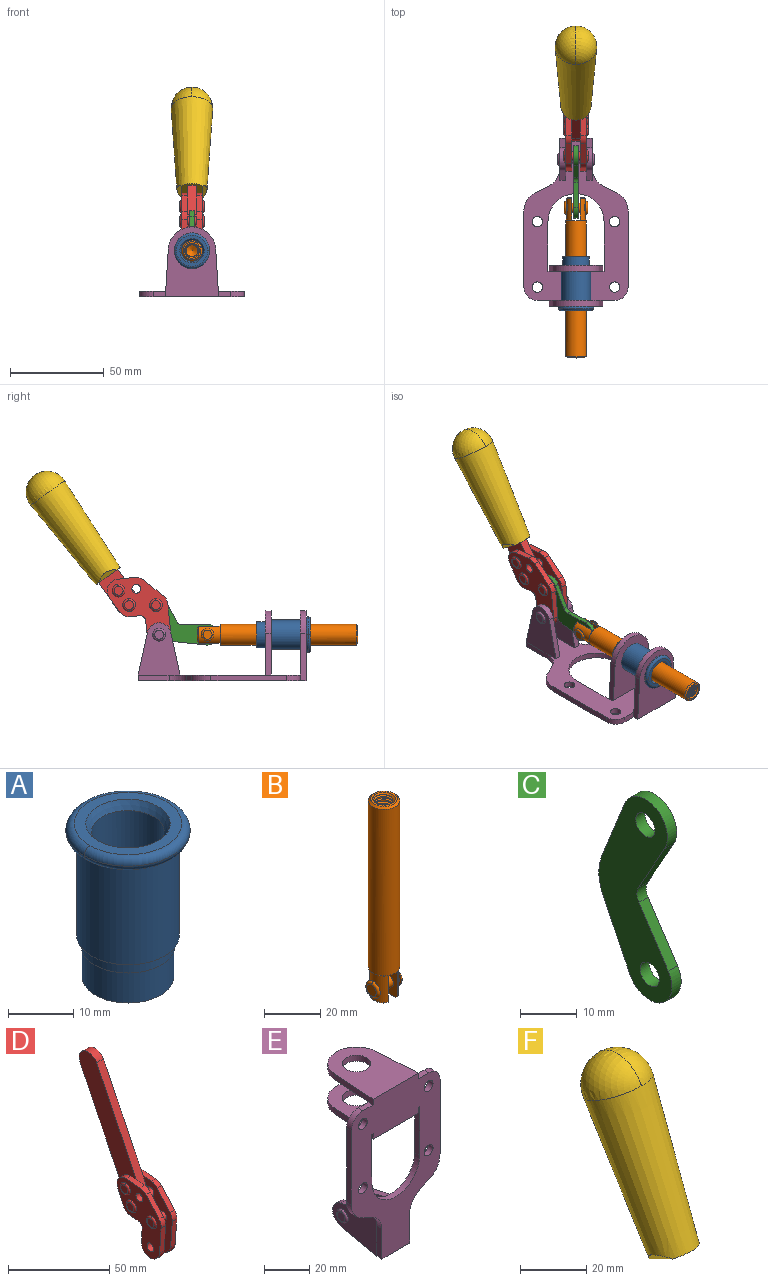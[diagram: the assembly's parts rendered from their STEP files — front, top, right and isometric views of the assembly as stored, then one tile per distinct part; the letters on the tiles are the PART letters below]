
ASSEMBLY  parts=6 mates=6
PART A: 15 faces, bbox 20.6x20.6x28.7 mm
  f0: torus R=8.26mm, axis (0,0,1), area 56.8mm2, adj f1,f10,f12
  f1: torus R=8.26mm, axis (0,0,1), area 56.8mm2, adj f0,f6,f13
  f2: cylinder r=5.59mm len=25.91mm, axis (0,0,1), area 909.6mm2, adj f3,f4
  f3: cone r=6.86mm half-angle=45deg, axis (0,0,-1), area 70.2mm2, adj f2,f14
  f4: cone r=6.47mm half-angle=30deg, axis (0,0,1), area 66.7mm2, adj f2,f13
  f5: cylinder r=7.04mm len=14.07mm, axis (0,0,1), area 252.6mm2, adj f11,f14
  f6: torus R=8.26mm, axis (0,0,1), area 56.8mm2, adj f1,f12,f13
  f7: cylinder r=7.16mm len=14.33mm, axis (0,0,1), area 91.5mm2, adj f9,f11
  f8: cylinder r=7.86mm len=18.42mm, axis (0,0,1), area 909.6mm2, adj f9,f10
  f9: plane 15.72x15.72mm, normal (0,0,-1), area 33mm2, adj f7,f8
  f10: plane 16.51x16.51mm, normal (0,0,-1), area 19.9mm2, adj f0,f8,f12
  f11: plane 14.33x14.33mm, normal (0,0,-1), area 5.7mm2, adj f5,f7
  f12: torus R=8.26mm, axis (0,0,1), area 56.8mm2, adj f0,f6,f10
  f13: plane 16.51x16.51mm, normal (0,0,1), area 82.7mm2, adj f1,f4,f6
  f14: plane 14.07x14.07mm, normal (0,0,-1), area 7.8mm2, adj f3,f5
PART B: 48 faces, bbox 12.6x11.1x86.1 mm
  f0: torus R=2.41mm, axis (-1,0,0), area 15mm2, adj f30,f32,f34
  f1: torus R=2.41mm, axis (-1,0,0), area 15mm2, adj f29,f31,f33
  f2: cylinder r=5.54mm len=72.39mm, axis (0,0,1), area 2518.5mm2, adj f3,f4,f42,f43
  f3: cone r=5.54mm half-angle=45deg, axis (0,0,1), area 7.6mm2, adj f2,f5,f41
  f4: cone r=5.54mm half-angle=45deg, axis (0,0,-1), area 34.9mm2, adj f2,f39
  f5: cylinder r=5.08mm len=11.48mm, axis (0,0,1), area 108.3mm2, adj f3,f7,f8,f41
  f6: cylinder r=2.41mm len=4.83mm, axis (-1,0,0), area 71.2mm2, adj f40,f41
  f7: cylinder r=2.41mm len=4.83mm, axis (-1,0,0), area 7.6mm2, adj f5,f34
  f8: cone r=5.08mm half-angle=45deg, axis (0,0,1), area 10.6mm2, adj f5,f37,f41
  f9: cone r=3.98mm half-angle=45deg, axis (0,0,1), area 17.6mm2, adj f27,f39,f45,f46,f47
  f10: cylinder r=2.41mm len=4.83mm, axis (-1,0,0), area 7.6mm2, adj f33,f38
  f11: cylinder r=3.2mm len=6.4mm, axis (0,0,1), area 78.4mm2, adj f12,f28,f44,f45,f47
  f12: cylinder r=3.2mm len=6.4mm, axis (0,0,1), area 10.5mm2, adj f11,f13,f45,f47
  f13: cylinder r=3.2mm len=6.4mm, axis (0,0,1), area 10.5mm2, adj f12,f14,f45,f47
  f14: cylinder r=3.2mm len=6.4mm, axis (0,0,1), area 10.5mm2, adj f13,f15,f45,f47
  f15: cylinder r=3.2mm len=6.4mm, axis (0,0,1), area 10.5mm2, adj f14,f16,f45,f47
  f16: cylinder r=3.2mm len=6.4mm, axis (0,0,1), area 10.5mm2, adj f15,f17,f45,f47
  f17: cylinder r=3.2mm len=6.4mm, axis (0,0,1), area 10.5mm2, adj f16,f18,f45,f47
  f18: cylinder r=3.2mm len=6.4mm, axis (0,0,1), area 10.5mm2, adj f17,f19,f45,f47
  f19: cylinder r=3.2mm len=6.4mm, axis (0,0,1), area 10.5mm2, adj f18,f20,f45,f47
  f20: cylinder r=3.2mm len=6.4mm, axis (0,0,1), area 10.5mm2, adj f19,f21,f45,f47
  f21: cylinder r=3.2mm len=6.4mm, axis (0,0,1), area 10.5mm2, adj f20,f22,f45,f47
  f22: cylinder r=3.2mm len=6.4mm, axis (0,0,1), area 10.5mm2, adj f21,f23,f45,f47
  f23: cylinder r=3.2mm len=6.4mm, axis (0,0,1), area 10.5mm2, adj f22,f24,f45,f47
  f24: cylinder r=3.2mm len=6.4mm, axis (0,0,1), area 10.5mm2, adj f23,f25,f45,f47
  f25: cylinder r=3.2mm len=6.4mm, axis (0,0,1), area 10.5mm2, adj f24,f26,f45,f47
  f26: cylinder r=3.2mm len=6.4mm, axis (0,0,1), area 10.5mm2, adj f25,f27,f45,f47
  f27: cylinder r=3.2mm len=6.4mm, axis (0,0,1), area 7.4mm2, adj f9,f26,f45,f47
  f28: cone r=3.2mm half-angle=60deg, axis (0,0,1), area 37.2mm2, adj f11
  f29: plane 4.83x4.83mm, normal (-1,0,0), area 18.3mm2, adj f1,f31
  f30: plane 4.83x4.83mm, normal (1,0,0), area 18.3mm2, adj f0,f32
  f31: torus R=2.41mm, axis (-1,0,0), area 15mm2, adj f1,f29,f33
  f32: torus R=2.41mm, axis (-1,0,0), area 15mm2, adj f0,f30,f34
  f33: plane 6.83x6.83mm, normal (1,0,0), area 18.3mm2, adj f1,f10,f31
  f34: plane 6.83x6.83mm, normal (-1,0,0), area 18.3mm2, adj f0,f7,f32
  f35: cone r=5.08mm half-angle=45deg, axis (0,0,1), area 10.6mm2, adj f36,f38,f40
  f36: plane 7.25x1.97mm, normal (0,0,-1), area 10mm2, adj f35,f40
  f37: plane 7.25x1.97mm, normal (0,0,-1), area 10mm2, adj f8,f41
  f38: cylinder r=5.08mm len=11.48mm, axis (0,0,1), area 108.3mm2, adj f10,f35,f40,f42
  f39: plane 9.55x9.55mm, normal (0,0,1), area 22mm2, adj f4,f9
  f40: plane 12.76x10.09mm, normal (1,0,0), area 95.7mm2, adj f6,f35,f36,f38,f42,f43
  f41: plane 12.76x10.09mm, normal (-1,0,0), area 95.7mm2, adj f3,f5,f6,f8,f37,f43
  f42: cone r=5.54mm half-angle=45deg, axis (0,0,1), area 7.6mm2, adj f2,f38,f40
  f43: plane 11.07x4.7mm, normal (0,0,-1), area 50.4mm2, adj f2,f40,f41
  f44: plane 0.89x0.62mm, normal (-1,0,0), area 0.3mm2, adj f11,f45,f46,f47
  f45: bspline ~24.8x7.63mm, area 266.6mm2, adj f9,f11,f12,f13,f14,f15,f16,f17
  f46: bspline ~24.87x7.63mm, area 73.6mm2, adj f9,f44,f45,f47
  f47: bspline ~24.98x7.63mm, area 272.5mm2, adj f9,f11,f12,f13,f14,f15,f16,f17
PART C: 12 faces, bbox 2.3x18.2x42.8 mm
  f0: cylinder r=2.4mm len=4.8mm, axis (1,0,0), area 34.9mm2, adj f4,f11
  f1: cylinder r=10.41mm len=8.47mm, axis (1,0,0), area 20.2mm2, adj f4,f9,f10,f11
  f2: cylinder r=3.05mm len=3.16mm, axis (1,0,0), area 7.7mm2, adj f4,f6,f7,f11
  f3: cylinder r=2.4mm len=4.8mm, axis (1,0,0), area 34.9mm2, adj f4,f11
  f4: plane 42.81x18.23mm, normal (-1,0,0), area 414.1mm2, adj f0,f1,f2,f3,f5,f6,f7,f8
  f5: cylinder r=5.54mm len=10.67mm, axis (1,0,0), area 41.8mm2, adj f4,f6,f10,f11
  f6: plane 11.66x6.53mm, normal (0,-0.87,-0.49), area 30.9mm2, adj f2,f4,f5,f11
  f7: plane 11.17x7.33mm, normal (0,-0.84,0.55), area 30.9mm2, adj f2,f4,f8,f11
  f8: cylinder r=5.54mm len=10.51mm, axis (1,0,0), area 41.8mm2, adj f4,f7,f9,f11
  f9: plane 13.67x6.67mm, normal (0,0.9,-0.44), area 35.1mm2, adj f1,f4,f8,f11
  f10: plane 14.1x5.7mm, normal (0,0.93,0.37), area 35.1mm2, adj f1,f4,f5,f11
  f11: plane 42.81x18.23mm, normal (1,0,0), area 414.1mm2, adj f0,f1,f2,f3,f5,f6,f7,f8
PART D: 59 faces, bbox 12.9x60.2x99.6 mm
  f0: torus R=2.39mm, axis (-1,0,0), area 14.9mm2, adj f20,f43,f51
  f1: torus R=2.39mm, axis (-1,0,0), area 14.9mm2, adj f19,f42,f51
  f2: torus R=2.39mm, axis (-1,0,0), area 14.9mm2, adj f18,f35,f51
  f3: torus R=2.39mm, axis (-1,0,0), area 14.9mm2, adj f14,f17,f23
  f4: torus R=2.39mm, axis (-1,0,0), area 14.9mm2, adj f13,f16,f23
  f5: torus R=2.39mm, axis (-1,0,0), area 14.9mm2, adj f12,f15,f23
  f6: cylinder r=2.39mm len=4.78mm, axis (1,0,0), area 46.5mm2, adj f48,f50,f51
  f7: cylinder r=2.39mm len=4.78mm, axis (1,0,0), area 46.5mm2, adj f50,f51
  f8: cylinder r=6.35mm len=12.68mm, axis (1,0,0), area 61.8mm2, adj f38,f39,f50,f51
  f9: cylinder r=2.39mm len=4.78mm, axis (-1,0,0), area 70.5mm2, adj f46,f50
  f10: cylinder r=2.39mm len=4.78mm, axis (-1,0,0), area 46.5mm2, adj f23,f45,f46
  f11: cylinder r=2.39mm len=4.78mm, axis (-1,0,0), area 46.5mm2, adj f23,f46
  f12: plane 4.78x4.78mm, normal (1,0,0), area 17.9mm2, adj f5,f15
  f13: plane 4.78x4.78mm, normal (1,0,0), area 17.9mm2, adj f4,f16
  f14: plane 4.78x4.78mm, normal (1,0,0), area 17.9mm2, adj f3,f17
  f15: torus R=2.39mm, axis (-1,0,0), area 14.9mm2, adj f5,f12,f23
  f16: torus R=2.39mm, axis (-1,0,0), area 14.9mm2, adj f4,f13,f23
  f17: torus R=2.39mm, axis (-1,0,0), area 14.9mm2, adj f3,f14,f23
  f18: plane 4.78x4.78mm, normal (-1,0,0), area 17.9mm2, adj f2,f35
  f19: plane 4.78x4.78mm, normal (-1,0,0), area 17.9mm2, adj f1,f42
  f20: plane 4.78x4.78mm, normal (-1,0,0), area 17.9mm2, adj f0,f43
  f21: plane 2.26x0.2mm, normal (1,0,0), area 0.2mm2, adj f31,f44
  f22: plane 2.26x0.2mm, normal (-1,0,0), area 0.2mm2, adj f41,f44
  f23: plane 39.37x30.77mm, normal (1,0,0), area 565.5mm2, adj f3,f4,f5,f10,f11,f15,f16,f17
  f24: cylinder r=6.1mm len=4.15mm, axis (-1,0,0), area 14.7mm2, adj f23,f25,f32,f46
  f25: plane 10.25x9.01mm, normal (0,-0.75,0.66), area 42.3mm2, adj f23,f24,f26,f46
  f26: cylinder r=6.35mm len=4.64mm, axis (-1,0,0), area 15.6mm2, adj f23,f25,f27,f46
  f27: plane 15.84x3.1mm, normal (0,-1,-0.07), area 49.2mm2, adj f23,f26,f28,f46
  f28: cylinder r=6.35mm len=12.68mm, axis (-1,0,0), area 61.8mm2, adj f23,f27,f29,f46
  f29: plane 8.11x3.1mm, normal (0,1,0.07), area 25.2mm2, adj f23,f28,f30,f46
  f30: cylinder r=3.05mm len=3.25mm, axis (-1,0,0), area 14.8mm2, adj f23,f29,f31,f46
  f31: plane 5.99x3.1mm, normal (0,0.07,-1), area 18.6mm2, adj f21,f23,f30,f44,f46
  f32: plane 9.5x3.1mm, normal (0,-0.07,1), area 29.5mm2, adj f23,f24,f33,f46,f47
  f33: cylinder r=6.1mm len=8.63mm, axis (-1,0,0), area 39.1mm2, adj f23,f32,f34,f47
  f34: plane 8.65x3.96mm, normal (0,0.91,-0.42), area 29.5mm2, adj f23,f33,f44,f47
  f35: torus R=2.39mm, axis (-1,0,0), area 14.9mm2, adj f2,f18,f51
  f36: plane 10.25x9.01mm, normal (0,-0.75,0.66), area 42.3mm2, adj f37,f49,f50,f51
  f37: cylinder r=6.35mm len=4.64mm, axis (1,0,0), area 15.6mm2, adj f36,f38,f50,f51
  f38: plane 15.84x3.1mm, normal (0,-1,-0.07), area 49.2mm2, adj f8,f37,f50,f51
  f39: plane 8.11x3.1mm, normal (0,1,0.07), area 25.2mm2, adj f8,f40,f50,f51
  f40: cylinder r=3.05mm len=3.25mm, axis (1,0,0), area 14.8mm2, adj f39,f41,f50,f51
  f41: plane 5.99x3.1mm, normal (0,0.07,-1), area 18.6mm2, adj f22,f40,f44,f50,f51
  f42: torus R=2.39mm, axis (-1,0,0), area 14.9mm2, adj f1,f19,f51
  f43: torus R=2.39mm, axis (-1,0,0), area 14.9mm2, adj f0,f20,f51
  f44: cylinder r=6.35mm len=12.12mm, axis (-1,0,0), area 128.9mm2, adj f21,f22,f23,f31,f34,f41,f46,f47
  f45: plane 2.65x1.35mm, normal (1,0,0), area 1mm2, adj f10,f55
  f46: plane 39.08x20.42mm, normal (-1,0,0), area 412.5mm2, adj f9,f10,f11,f24,f25,f26,f27,f28
  f47: plane 77.62x39.82mm, normal (1,0,0), area 850mm2, adj f32,f33,f34,f44,f53,f54,f55
  f48: plane 2.65x1.35mm, normal (-1,0,0), area 1mm2, adj f6,f55
  f49: cylinder r=6.1mm len=4.15mm, axis (1,0,0), area 14.7mm2, adj f36,f50,f51,f56
  f50: plane 39.08x20.42mm, normal (1,0,0), area 412.5mm2, adj f6,f7,f8,f9,f36,f37,f38,f39
  f51: plane 39.37x30.77mm, normal (-1,0,0), area 565.5mm2, adj f0,f1,f2,f6,f7,f8,f35,f36
  f52: plane 8.65x3.96mm, normal (0,0.91,-0.42), area 29.5mm2, adj f44,f51,f57,f58
  f53: plane 68.49x33.4mm, normal (0,0.9,-0.44), area 358.1mm2, adj f44,f47,f54,f58
  f54: cylinder r=6.35mm len=12.06mm, axis (1,0,0), area 93.7mm2, adj f47,f53,f55,f58
  f55: plane 68.49x33.4mm, normal (0,-0.9,0.44), area 358.1mm2, adj f44,f45,f46,f47,f48,f50,f54,f58
  f56: plane 9.5x3.1mm, normal (0,-0.07,1), area 29.5mm2, adj f49,f50,f51,f57,f58
  f57: cylinder r=6.1mm len=8.63mm, axis (1,0,0), area 39.1mm2, adj f51,f52,f56,f58
  f58: plane 77.62x39.82mm, normal (-1,0,0), area 850mm2, adj f44,f52,f53,f54,f55,f56,f57
PART E: 55 faces, bbox 55.7x37.4x89.8 mm
  f0: torus R=2.41mm, axis (-1,0,0), area 15mm2, adj f11,f15,f25
  f1: torus R=2.41mm, axis (-1,0,0), area 15mm2, adj f10,f12,f22
  f2: cylinder r=2.78mm len=5.56mm, axis (0,-1,0), area 54.2mm2, adj f30,f54
  f3: cylinder r=14.99mm len=29.97mm, axis (0,-1,0), area 145.9mm2, adj f30,f49,f53,f54
  f4: cylinder r=2.78mm len=5.56mm, axis (0,-1,0), area 54.2mm2, adj f30,f54
  f5: cylinder r=2.78mm len=5.56mm, axis (0,-1,0), area 54.2mm2, adj f30,f54
  f6: cylinder r=2.78mm len=5.56mm, axis (0,-1,0), area 54.2mm2, adj f30,f54
  f7: cylinder r=6.35mm len=12.7mm, axis (0,0,1), area 123.6mm2, adj f27,f51
  f8: cylinder r=6.35mm len=12.7mm, axis (0,0,-1), area 124.7mm2, adj f21,f35
  f9: cylinder r=2.41mm len=11.18mm, axis (-1,0,0), area 169.4mm2, adj f16,f19
  f10: plane 4.83x4.83mm, normal (1,0,0), area 18.3mm2, adj f1,f12
  f11: plane 4.83x4.83mm, normal (-1,0,0), area 18.3mm2, adj f0,f15
  f12: torus R=2.41mm, axis (-1,0,0), area 15mm2, adj f1,f10,f22
  f13: cylinder r=6.35mm len=12.41mm, axis (1,0,0), area 53.4mm2, adj f18,f19,f22,f23
  f14: cylinder r=6.35mm len=12.41mm, axis (-1,0,0), area 53.4mm2, adj f16,f17,f24,f25
  f15: torus R=2.41mm, axis (-1,0,0), area 15mm2, adj f0,f11,f25
  f16: plane 27.86x22.35mm, normal (1,0,0), area 425.4mm2, adj f9,f14,f17,f24,f30
  f17: plane 22.86x4.97mm, normal (0,0.21,0.98), area 72.5mm2, adj f14,f16,f25,f30
  f18: plane 22.86x4.97mm, normal (0,0.21,0.98), area 72.5mm2, adj f13,f19,f22,f30
  f19: plane 27.86x22.35mm, normal (-1,0,0), area 425.4mm2, adj f9,f13,f18,f23,f30
  f20: cylinder r=12.7mm len=25.35mm, axis (0,0,-1), area 119.8mm2, adj f21,f34,f35,f36
  f21: plane 34.21x28.07mm, normal (0,0,-1), area 702.4mm2, adj f8,f20,f30,f34,f36
  f22: plane 27.96x22.45mm, normal (1,0,0), area 407.2mm2, adj f1,f12,f13,f18,f23,f30,f42,f43
  f23: plane 22.86x4.97mm, normal (0,0.21,-0.98), area 72.5mm2, adj f13,f19,f22,f44
  f24: plane 22.86x4.97mm, normal (0,0.21,-0.98), area 72.5mm2, adj f14,f16,f25,f44
  f25: plane 27.86x22.35mm, normal (-1,0,0), area 407.1mm2, adj f0,f14,f15,f17,f24,f30,f45,f46
  f26: plane 3.1x0.95mm, normal (0,0,-1), area 2.7mm2, adj f30,f49,f50,f54
  f27: plane 34.21x28.07mm, normal (0,0,1), area 702.4mm2, adj f7,f28,f30,f50,f52
  f28: cylinder r=12.7mm len=25.35mm, axis (0,0,1), area 118.8mm2, adj f27,f50,f51,f52
  f29: plane 3.1x0.95mm, normal (0,0,-1), area 2.7mm2, adj f30,f52,f53,f54
  f30: plane 86.54x55.63mm, normal (0,1,0), area 2362.9mm2, adj f2,f3,f4,f5,f6,f16,f17,f18
  f31: plane 40.56x3.1mm, normal (-1,0,0), area 125.7mm2, adj f30,f32,f48,f54
  f32: cylinder r=7.11mm len=7.11mm, axis (0,-1,0), area 34.6mm2, adj f30,f31,f33,f54
  f33: plane 6.67x3.1mm, normal (0,0,1), area 20.4mm2, adj f30,f32,f34,f54
  f34: plane 25.39x3.13mm, normal (-1,0.06,0), area 79.5mm2, adj f20,f21,f33,f35,f54
  f35: plane 37.31x28.45mm, normal (0,0,1), area 789.9mm2, adj f8,f20,f34,f36,f54
  f36: plane 25.39x3.13mm, normal (1,0.06,0), area 79.5mm2, adj f20,f21,f35,f37,f54
  f37: plane 6.67x3.1mm, normal (0,0,1), area 20.4mm2, adj f30,f36,f38,f54
  f38: cylinder r=7.11mm len=7.11mm, axis (0,-1,0), area 34.6mm2, adj f30,f37,f39,f54
  f39: plane 40.56x3.1mm, normal (1,0,0), area 125.7mm2, adj f30,f38,f40,f54
  f40: cylinder r=11.18mm len=10.16mm, axis (0,-1,0), area 39.5mm2, adj f30,f39,f41,f54
  f41: plane 6.09x3.1mm, normal (0.42,0,-0.91), area 20.8mm2, adj f30,f40,f42,f54
  f42: cylinder r=11.18mm len=9.41mm, axis (0,-1,0), area 37.2mm2, adj f22,f30,f41,f43,f54
  f43: plane 16.5x3.1mm, normal (1,0,0), area 51.1mm2, adj f22,f42,f44,f54
  f44: plane 17.37x3.1mm, normal (0,0,-1), area 53.8mm2, adj f23,f24,f30,f43,f45,f54
  f45: plane 16.5x3.1mm, normal (-1,0,0), area 51.1mm2, adj f25,f44,f46,f54
  f46: cylinder r=11.18mm len=9.41mm, axis (0,-1,0), area 37.2mm2, adj f25,f30,f45,f47,f54
  f47: plane 6.09x3.1mm, normal (-0.42,0,-0.91), area 20.8mm2, adj f30,f46,f48,f54
  f48: cylinder r=11.18mm len=10.16mm, axis (0,-1,0), area 39.5mm2, adj f30,f31,f47,f54
  f49: plane 26.54x3.1mm, normal (-1,0,0), area 82.3mm2, adj f3,f26,f30,f54
  f50: plane 25.39x3.1mm, normal (1,0.06,0), area 78.8mm2, adj f26,f27,f28,f51,f54
  f51: plane 37.31x28.45mm, normal (0,0,-1), area 789.9mm2, adj f7,f28,f50,f52,f54
  f52: plane 25.39x3.1mm, normal (-1,0.06,0), area 78.8mm2, adj f27,f28,f29,f51,f54
  f53: plane 26.54x3.1mm, normal (1,0,0), area 82.3mm2, adj f3,f29,f30,f54
  f54: plane 89.66x55.63mm, normal (0,-1,0), area 2678.5mm2, adj f2,f3,f4,f5,f6,f26,f29,f31
PART F: 11 faces, bbox 22.3x42.6x64.5 mm
  f0: sphere r=11.13mm, area 411.4mm2, adj f1,f8
  f1: cone r=11.11mm half-angle=3.3deg, axis (0,0.44,0.9), area 3251.8mm2, adj f0,f7,f8,f9,f10
  f2: cylinder r=6.16mm len=11.7mm, axis (1,0,0), area 89.5mm2, adj f3,f4,f5,f6
  f3: plane 60.23x36.75mm, normal (-1,0,0), area 763.6mm2, adj f2,f4,f6,f10
  f4: plane 51.37x25.05mm, normal (0,0.9,-0.44), area 264.2mm2, adj f2,f3,f5,f10
  f5: plane 60.23x36.75mm, normal (1,0,0), area 763.6mm2, adj f2,f4,f6,f10
  f6: plane 51.37x25.05mm, normal (0,-0.9,0.44), area 264.2mm2, adj f2,f3,f5,f10
  f7: plane 9.95x5.95mm, normal (0.71,-0.31,-0.64), area 25.8mm2, adj f1,f10
  f8: sphere r=11.13mm, area 411.4mm2, adj f0,f1
  f9: plane 9.95x5.95mm, normal (-0.71,-0.31,-0.64), area 25.8mm2, adj f1,f10
  f10: plane 14.27x11.38mm, normal (0,-0.44,-0.9), area 106.7mm2, adj f1,f3,f4,f5,f6,f7,f9
PLACE A rot(axis=(1,0,0),90deg) t=(0,1.44,0)mm
PLACE B rot(axis=(1,0,0),90deg) t=(0,22.91,0)mm
PLACE C rot(axis=(-1,0,0),58.2deg) t=(0,8.86,53.16)mm
PLACE D rot(axis=(-1,0,0),10deg) t=(0,14.66,60.49)mm
PLACE E rot(axis=(1,0,0),90deg) t=(0,1.23,0)mm fixed
PLACE F rot(axis=(-1,0,0),10deg) t=(-0.04,14.66,60.49)mm
MATE fastened F.f2 <-> D.f54  axis (1,0,0) through (-2.35,94.13,102.1)mm
MATE revolute C.f5 <-> D.f4  axis (1,0,0) through (0,34.98,40.4)mm
MATE fastened A.f2 <-> E.f7  axis (0,-1,0) through (0,-45.97,24.61)mm
MATE revolute C.f3 <-> B.f6  axis (1,0,0) through (0,7.44,24.61)mm
MATE slider A.f12 <-> B.f2  axis (0,-1,0) through (0,-47.5,24.61)mm
MATE revolute E.f0 <-> D.f7  axis (-1,0,0) through (0,33.32,24.61)mm
